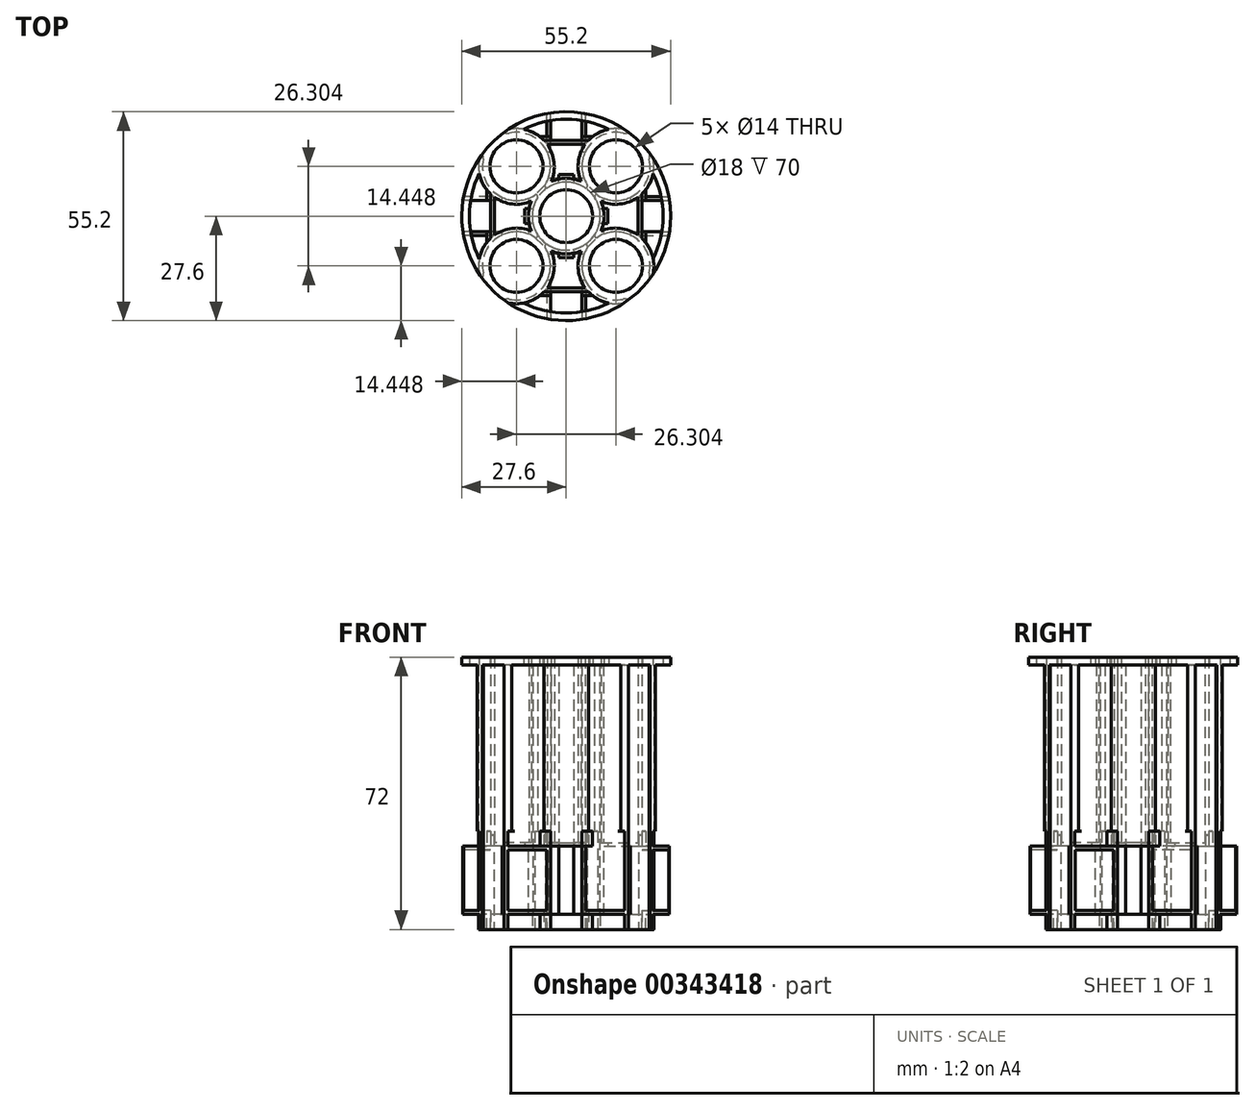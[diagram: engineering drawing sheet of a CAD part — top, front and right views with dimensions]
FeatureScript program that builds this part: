
annotation { "Feature Type Name" : "Feature", "Feature Type Description" : "" }
export const myFeature = defineFeature(function(context is Context, id is Id, definition is map)
    precondition{}
    {
        {
            var Q0;
            Q0=qCreatedBy(makeId("Top.planeOp"),FACE);
            var sketch = newSketch(context, id + "F0", { "sketchPlane" : qUnion([Q0])});
            skCircle(sketch, "E0", {"center": v(0, 0) * mm, "radius": 27.6 * mm});
            skCircle(sketch, "E1.0", {"center": v(0, 0) * mm, "radius": 28.6 * mm, "construction": true});
            skSolve(sketch);
        }
        {
            var Q0;
            Q0=qCreatedBy(makeId("Top.planeOp"),FACE);
            var sketch = newSketch(context, id + "F1", { "sketchPlane" : qUnion([Q0])});
            skCircle(sketch, "E2", {"center": v(13.15, 13.15) * mm, "radius": 9 * mm, "construction": true});
            skLineSegment(sketch, "E3", {"start": v(13.15, 13.15) * mm, "end": v(13.15, 0) * mm, "construction": true});
            skLineSegment(sketch, "E4", {"start": v(13.15, 13.15) * mm, "end": v(0, 13.15) * mm, "construction": true});
            skCircle(sketch, "E5.0", {"center": v(13.15, 13.15) * mm, "radius": 10 * mm, "construction": true});
            skCircle(sketch, "E6.1.0", {"center": v(-13.15, 13.15) * mm, "radius": 9 * mm, "construction": true});
            skCircle(sketch, "E6.1.1", {"center": v(-13.15, 13.15) * mm, "radius": 10 * mm, "construction": true});
            skCircle(sketch, "E6.2.0", {"center": v(-13.15, -13.15) * mm, "radius": 9 * mm, "construction": true});
            skCircle(sketch, "E6.2.1", {"center": v(-13.15, -13.15) * mm, "radius": 10 * mm, "construction": true});
            skCircle(sketch, "E6.3.0", {"center": v(13.15, -13.15) * mm, "radius": 9 * mm, "construction": true});
            skCircle(sketch, "E6.3.1", {"center": v(13.15, -13.15) * mm, "radius": 10 * mm, "construction": true});
            skPoint(sketch, "E6.center", {"position": v(0, 0) * mm});
            skCircle(sketch, "E7.0", {"center": v(0, 0) * mm, "radius": 9 * mm, "construction": true});
            skCircle(sketch, "E8.0", {"center": v(0, 0) * mm, "radius": 10 * mm, "construction": true});
            skSolve(sketch);
        }
        {
            var Q0;
            Q0=qCreatedBy(makeId("Top.planeOp"),FACE);
            var sketch = newSketch(context, id + "F2", { "sketchPlane" : qUnion([Q0])});
            skLineSegment(sketch, "E9.top", {"start": v(-4.13, 27) * mm, "end": v(4.12, 27) * mm, "construction": true});
            skLineSegment(sketch, "E9.left", {"start": v(-4.12, 10) * mm, "end": v(-4.13, 27) * mm, "construction": true});
            skLineSegment(sketch, "E9.right", {"start": v(4.13, 10) * mm, "end": v(4.13, 27) * mm, "construction": true});
            skPoint(sketch, "E9.middle", {"position": v(0, 18.5) * mm});
            skLineSegment(sketch, "E10", {"start": v(5.86, 20) * mm, "end": v(-5.86, 20) * mm, "construction": true});
            skLineSegment(sketch, "E11.top", {"start": v(3, 30) * mm, "end": v(-3, 30) * mm, "construction": true});
            skLineSegment(sketch, "E11.left", {"start": v(3, 27) * mm, "end": v(3, 30) * mm, "construction": true});
            skLineSegment(sketch, "E11.right", {"start": v(-3, 27) * mm, "end": v(-3, 30) * mm, "construction": true});
            skPoint(sketch, "E11.middle", {"position": v(0, 28.5) * mm});
            skLineSegment(sketch, "E12.1.4", {"start": v(-19, -5) * mm, "end": v(-19, -5) * mm});
            skLineSegment(sketch, "E12.2.4", {"start": v(5, -19) * mm, "end": v(5, -19) * mm});
            skLineSegment(sketch, "E12.3.4", {"start": v(19, 5) * mm, "end": v(19, 5) * mm});
            skLineSegment(sketch, "E13", {"start": v(-6.95, 21) * mm, "end": v(6.95, 21) * mm, "construction": true});
            skLineSegment(sketch, "E14", {"start": v(5.13, 21) * mm, "end": v(5.13, 27.12) * mm, "construction": true});
            skLineSegment(sketch, "E15.MirrorCS", {"start": v(-5.13, 21) * mm, "end": v(-5.13, 27.12) * mm, "construction": true});
            skLineSegment(sketch, "E16.top", {"start": v(2, 11) * mm, "end": v(-2, 11) * mm, "construction": true});
            skLineSegment(sketch, "E16.left", {"start": v(2, 10) * mm, "end": v(2, 11) * mm, "construction": true});
            skLineSegment(sketch, "E16.right", {"start": v(-2, 10) * mm, "end": v(-2, 11) * mm, "construction": true});
            skPoint(sketch, "E16.middle", {"position": v(0, 10.5) * mm});
            skLineSegment(sketch, "E17", {"start": v(-2, 10) * mm, "end": v(-2, 8.77) * mm, "construction": true});
            skLineSegment(sketch, "E18", {"start": v(2, 10) * mm, "end": v(2, 8.77) * mm, "construction": true});
            skLineSegment(sketch, "E19", {"start": v(4.13, 10) * mm, "end": v(-4.12, 10) * mm, "construction": true});
            skArc(sketch, "E20", {"start": v(-2, 8.77) * mm, "mid": v(0, 6.77) * mm, "end": v(2, 8.77) * mm, "construction": true});
            skLineSegment(sketch, "E21", {"start": v(-5.04, 19) * mm, "end": v(5.04, 19) * mm, "construction": true});
            skSolve(sketch);
        }
        {
            var Q0;
            Q0=qCreatedBy(makeId("Top.planeOp"),FACE);
            var sketch = newSketch(context, id + "F3", { "sketchPlane" : qUnion([Q0])});
            skArc(sketch, "E22", {"start": v(17.22, 22.83) * mm, "mid": v(20.22, 20.22) * mm, "end": v(22.83, 17.22) * mm});
            skArc(sketch, "E23", {"start": v(15.01, 21.96) * mm, "mid": v(5.75, 18.27) * mm, "end": v(5.57, 8.3) * mm});
            skPoint(sketch, "E24", {"position": v(5.57, 8.3) * mm});
            skPoint(sketch, "E25", {"position": v(8.3, 5.57) * mm});
            skLineSegment(sketch, "E26", {"start": v(5.57, 8.3) * mm, "end": v(8.3, 5.57) * mm});
            skArc(sketch, "E27.trimOffspring", {"start": v(8.3, 5.57) * mm, "mid": v(18.27, 5.75) * mm, "end": v(21.96, 15.01) * mm});
            skLineSegment(sketch, "E28", {"start": v(21.96, 15.01) * mm, "end": v(22.78, 15.58) * mm, "construction": true});
            skLineSegment(sketch, "E29", {"start": v(15.01, 21.96) * mm, "end": v(15.58, 22.78) * mm, "construction": true});
            skArc(sketch, "E30", {"start": v(15.01, 21.96) * mm, "mid": v(16.25, 22.06) * mm, "end": v(17.22, 22.83) * mm});
            skArc(sketch, "E31", {"start": v(22.83, 17.22) * mm, "mid": v(22.06, 16.25) * mm, "end": v(21.96, 15.01) * mm});
            skPoint(sketch, "E32.1.0", {"position": v(-8.3, 5.57) * mm});
            skPoint(sketch, "E32.1.1", {"position": v(-5.57, 8.3) * mm});
            skArc(sketch, "E32.1.2", {"start": v(-5.57, 8.3) * mm, "mid": v(-5.75, 18.27) * mm, "end": v(-15.01, 21.96) * mm});
            skArc(sketch, "E32.1.3", {"start": v(-21.96, 15.01) * mm, "mid": v(-18.27, 5.75) * mm, "end": v(-8.3, 5.57) * mm});
            skLineSegment(sketch, "E32.1.4", {"start": v(-15.01, 21.96) * mm, "end": v(-15.58, 22.78) * mm, "construction": true});
            skArc(sketch, "E32.1.5", {"start": v(-21.96, 15.01) * mm, "mid": v(-22.06, 16.25) * mm, "end": v(-22.83, 17.22) * mm});
            skLineSegment(sketch, "E32.1.6", {"start": v(-21.96, 15.01) * mm, "end": v(-22.78, 15.58) * mm, "construction": true});
            skArc(sketch, "E32.1.7", {"start": v(-17.22, 22.83) * mm, "mid": v(-16.25, 22.06) * mm, "end": v(-15.01, 21.96) * mm});
            skArc(sketch, "E32.1.8", {"start": v(-22.83, 17.22) * mm, "mid": v(-20.22, 20.22) * mm, "end": v(-17.22, 22.83) * mm});
            skLineSegment(sketch, "E32.1.9", {"start": v(-8.3, 5.57) * mm, "end": v(-5.57, 8.3) * mm});
            skPoint(sketch, "E32.2.0", {"position": v(-5.57, -8.3) * mm});
            skPoint(sketch, "E32.2.1", {"position": v(-8.3, -5.57) * mm});
            skArc(sketch, "E32.2.2", {"start": v(-8.3, -5.57) * mm, "mid": v(-18.27, -5.75) * mm, "end": v(-21.96, -15.01) * mm});
            skArc(sketch, "E32.2.3", {"start": v(-15.01, -21.96) * mm, "mid": v(-5.75, -18.27) * mm, "end": v(-5.57, -8.3) * mm});
            skLineSegment(sketch, "E32.2.4", {"start": v(-21.96, -15.01) * mm, "end": v(-22.78, -15.58) * mm, "construction": true});
            skArc(sketch, "E32.2.5", {"start": v(-15.01, -21.96) * mm, "mid": v(-16.25, -22.06) * mm, "end": v(-17.22, -22.83) * mm});
            skLineSegment(sketch, "E32.2.6", {"start": v(-15.01, -21.96) * mm, "end": v(-15.58, -22.78) * mm, "construction": true});
            skArc(sketch, "E32.2.7", {"start": v(-22.83, -17.22) * mm, "mid": v(-22.06, -16.25) * mm, "end": v(-21.96, -15.01) * mm});
            skArc(sketch, "E32.2.8", {"start": v(-17.22, -22.83) * mm, "mid": v(-20.22, -20.22) * mm, "end": v(-22.83, -17.22) * mm});
            skLineSegment(sketch, "E32.2.9", {"start": v(-5.57, -8.3) * mm, "end": v(-8.3, -5.57) * mm});
            skPoint(sketch, "E32.3.0", {"position": v(8.3, -5.57) * mm});
            skPoint(sketch, "E32.3.1", {"position": v(5.57, -8.3) * mm});
            skArc(sketch, "E32.3.2", {"start": v(5.57, -8.3) * mm, "mid": v(5.75, -18.27) * mm, "end": v(15.01, -21.96) * mm});
            skArc(sketch, "E32.3.3", {"start": v(21.96, -15.01) * mm, "mid": v(18.27, -5.75) * mm, "end": v(8.3, -5.57) * mm});
            skLineSegment(sketch, "E32.3.4", {"start": v(15.01, -21.96) * mm, "end": v(15.58, -22.78) * mm, "construction": true});
            skArc(sketch, "E32.3.5", {"start": v(21.96, -15.01) * mm, "mid": v(22.06, -16.25) * mm, "end": v(22.83, -17.22) * mm});
            skLineSegment(sketch, "E32.3.6", {"start": v(21.96, -15.01) * mm, "end": v(22.78, -15.58) * mm, "construction": true});
            skArc(sketch, "E32.3.7", {"start": v(17.22, -22.83) * mm, "mid": v(16.25, -22.06) * mm, "end": v(15.01, -21.96) * mm});
            skArc(sketch, "E32.3.8", {"start": v(22.83, -17.22) * mm, "mid": v(20.22, -20.22) * mm, "end": v(17.22, -22.83) * mm});
            skLineSegment(sketch, "E32.3.9", {"start": v(8.3, -5.57) * mm, "end": v(5.57, -8.3) * mm});
            skCircle(sketch, "E33.0", {"center": v(0, 0) * mm, "radius": 9 * mm});
            skSolve(sketch);
        }
        {
            var Q0;
            Q0=qCreatedBy(makeId("Top.planeOp"),FACE);
            var sketch = newSketch(context, id + "F4", { "sketchPlane" : qUnion([Q0])});
            skLineSegment(sketch, "E34.0", {"start": v(-4.12, 20) * mm, "end": v(-4.13, 21) * mm});
            skLineSegment(sketch, "E35.0", {"start": v(4.13, 20) * mm, "end": v(4.13, 21) * mm});
            skPoint(sketch, "E36.0", {"position": v(0, 18.5) * mm});
            skLineSegment(sketch, "E37.0", {"start": v(4.13, 20) * mm, "end": v(-4.12, 20) * mm});
            skLineSegment(sketch, "E38.0", {"start": v(-6.95, 21) * mm, "end": v(-4.13, 21) * mm});
            skLineSegment(sketch, "E39.trimOffspring", {"start": v(4.13, 21) * mm, "end": v(6.95, 21) * mm});
            skArc(sketch, "E40.0", {"start": v(15.98, 23.72) * mm, "mid": v(0, 28.6) * mm, "end": v(-15.98, 23.72) * mm});
            skArc(sketch, "E41.0", {"start": v(15.42, 22.9) * mm, "mid": v(10.97, 22.91) * mm, "end": v(6.95, 21) * mm});
            skLineSegment(sketch, "E42", {"start": v(15.42, 22.9) * mm, "end": v(15.98, 23.72) * mm});
            skLineSegment(sketch, "E43", {"start": v(-15.42, 22.9) * mm, "end": v(-15.98, 23.72) * mm});
            skArc(sketch, "E44.trimOffspring", {"start": v(-6.95, 21) * mm, "mid": v(-10.97, 22.91) * mm, "end": v(-15.42, 22.9) * mm});
            skArc(sketch, "E45.1.0", {"start": v(-23.72, 15.98) * mm, "mid": v(-28.6, 0) * mm, "end": v(-23.72, -15.98) * mm});
            skLineSegment(sketch, "E45.1.1", {"start": v(-20, -4.12) * mm, "end": v(-21, -4.13) * mm});
            skLineSegment(sketch, "E45.1.2", {"start": v(-22.9, -15.42) * mm, "end": v(-23.72, -15.98) * mm});
            skArc(sketch, "E45.1.3", {"start": v(-21, -6.95) * mm, "mid": v(-22.91, -10.97) * mm, "end": v(-22.9, -15.42) * mm});
            skLineSegment(sketch, "E45.1.4", {"start": v(-21, -6.95) * mm, "end": v(-21, -4.13) * mm});
            skArc(sketch, "E45.1.5", {"start": v(-22.9, 15.42) * mm, "mid": v(-22.91, 10.97) * mm, "end": v(-21, 6.95) * mm});
            skPoint(sketch, "E45.1.6", {"position": v(-18.5, 0) * mm});
            skLineSegment(sketch, "E45.1.7", {"start": v(-20, 4.13) * mm, "end": v(-21, 4.13) * mm});
            skLineSegment(sketch, "E45.1.8", {"start": v(-20, 4.13) * mm, "end": v(-20, -4.12) * mm});
            skLineSegment(sketch, "E45.1.9", {"start": v(-21, 4.13) * mm, "end": v(-21, 6.95) * mm});
            skLineSegment(sketch, "E45.1.10", {"start": v(-20, 4.13) * mm, "end": v(-21, 4.13) * mm});
            skLineSegment(sketch, "E45.1.11", {"start": v(-22.9, 15.42) * mm, "end": v(-23.72, 15.98) * mm});
            skArc(sketch, "E45.2.0", {"start": v(-15.98, -23.72) * mm, "mid": v(0, -28.6) * mm, "end": v(15.98, -23.72) * mm});
            skLineSegment(sketch, "E45.2.1", {"start": v(4.12, -20) * mm, "end": v(4.12, -21) * mm});
            skLineSegment(sketch, "E45.2.2", {"start": v(15.42, -22.9) * mm, "end": v(15.98, -23.72) * mm});
            skArc(sketch, "E45.2.3", {"start": v(6.95, -21) * mm, "mid": v(10.97, -22.91) * mm, "end": v(15.42, -22.9) * mm});
            skLineSegment(sketch, "E45.2.4", {"start": v(6.95, -21) * mm, "end": v(4.12, -21) * mm});
            skArc(sketch, "E45.2.5", {"start": v(-15.42, -22.9) * mm, "mid": v(-10.97, -22.91) * mm, "end": v(-6.95, -21) * mm});
            skPoint(sketch, "E45.2.6", {"position": v(0, -18.5) * mm});
            skLineSegment(sketch, "E45.2.7", {"start": v(-4.13, -20) * mm, "end": v(-4.13, -21) * mm});
            skLineSegment(sketch, "E45.2.8", {"start": v(-4.13, -20) * mm, "end": v(4.12, -20) * mm});
            skLineSegment(sketch, "E45.2.9", {"start": v(-4.13, -21) * mm, "end": v(-6.95, -21) * mm});
            skLineSegment(sketch, "E45.2.10", {"start": v(-4.13, -20) * mm, "end": v(-4.13, -21) * mm});
            skLineSegment(sketch, "E45.2.11", {"start": v(-15.42, -22.9) * mm, "end": v(-15.98, -23.72) * mm});
            skArc(sketch, "E45.3.0", {"start": v(23.72, -15.98) * mm, "mid": v(28.6, 0) * mm, "end": v(23.72, 15.98) * mm});
            skLineSegment(sketch, "E45.3.1", {"start": v(20, 4.13) * mm, "end": v(21, 4.13) * mm});
            skLineSegment(sketch, "E45.3.2", {"start": v(22.9, 15.42) * mm, "end": v(23.72, 15.98) * mm});
            skArc(sketch, "E45.3.3", {"start": v(21, 6.95) * mm, "mid": v(22.91, 10.97) * mm, "end": v(22.9, 15.42) * mm});
            skLineSegment(sketch, "E45.3.4", {"start": v(21, 6.95) * mm, "end": v(21, 4.13) * mm});
            skArc(sketch, "E45.3.5", {"start": v(22.9, -15.42) * mm, "mid": v(22.91, -10.97) * mm, "end": v(21, -6.95) * mm});
            skPoint(sketch, "E45.3.6", {"position": v(18.5, 0) * mm});
            skLineSegment(sketch, "E45.3.7", {"start": v(20, -4.12) * mm, "end": v(21, -4.12) * mm});
            skLineSegment(sketch, "E45.3.8", {"start": v(20, -4.12) * mm, "end": v(20, 4.12) * mm});
            skLineSegment(sketch, "E45.3.9", {"start": v(21, -4.12) * mm, "end": v(21, -6.95) * mm});
            skLineSegment(sketch, "E45.3.10", {"start": v(20, -4.12) * mm, "end": v(21, -4.12) * mm});
            skLineSegment(sketch, "E45.3.11", {"start": v(22.9, -15.42) * mm, "end": v(23.72, -15.98) * mm});
            skSolve(sketch);
        }
        {
            var Q0;
            Q0=qCreatedBy(makeId("Top.planeOp"),FACE);
            var sketch = newSketch(context, id + "F5", { "sketchPlane" : qUnion([Q0])});
            skArc(sketch, "E46.0", {"start": v(-2, 8.77) * mm, "mid": v(0, 6.77) * mm, "end": v(2, 8.77) * mm});
            skLineSegment(sketch, "E47.0", {"start": v(2, 11) * mm, "end": v(-2, 11) * mm});
            skLineSegment(sketch, "E48.0", {"start": v(2, 10) * mm, "end": v(2, 11) * mm});
            skLineSegment(sketch, "E49.0", {"start": v(2, 10) * mm, "end": v(2, 8.77) * mm});
            skLineSegment(sketch, "E50.0", {"start": v(-2, 10) * mm, "end": v(-2, 8.77) * mm});
            skLineSegment(sketch, "E51.0", {"start": v(-2, 10) * mm, "end": v(-2, 11) * mm});
            skArc(sketch, "E52.1.0", {"start": v(-8.77, -2) * mm, "mid": v(-6.77, 0) * mm, "end": v(-8.77, 2) * mm});
            skLineSegment(sketch, "E52.1.1", {"start": v(-11, 2) * mm, "end": v(-11, -2) * mm});
            skLineSegment(sketch, "E52.1.2", {"start": v(-10, 2) * mm, "end": v(-11, 2) * mm});
            skLineSegment(sketch, "E52.1.3", {"start": v(-10, -2) * mm, "end": v(-11, -2) * mm});
            skLineSegment(sketch, "E52.1.4", {"start": v(-10, 2) * mm, "end": v(-8.77, 2) * mm});
            skLineSegment(sketch, "E52.1.5", {"start": v(-10, -2) * mm, "end": v(-8.77, -2) * mm});
            skArc(sketch, "E52.2.0", {"start": v(2, -8.77) * mm, "mid": v(0, -6.77) * mm, "end": v(-2, -8.77) * mm});
            skLineSegment(sketch, "E52.2.1", {"start": v(-2, -11) * mm, "end": v(2, -11) * mm});
            skLineSegment(sketch, "E52.2.2", {"start": v(-2, -10) * mm, "end": v(-2, -11) * mm});
            skLineSegment(sketch, "E52.2.3", {"start": v(2, -10) * mm, "end": v(2, -11) * mm});
            skLineSegment(sketch, "E52.2.4", {"start": v(-2, -10) * mm, "end": v(-2, -8.77) * mm});
            skLineSegment(sketch, "E52.2.5", {"start": v(2, -10) * mm, "end": v(2, -8.77) * mm});
            skArc(sketch, "E52.3.0", {"start": v(8.77, 2) * mm, "mid": v(6.77, 0) * mm, "end": v(8.77, -2) * mm});
            skLineSegment(sketch, "E52.3.1", {"start": v(11, -2) * mm, "end": v(11, 2) * mm});
            skLineSegment(sketch, "E52.3.2", {"start": v(10, -2) * mm, "end": v(11, -2) * mm});
            skLineSegment(sketch, "E52.3.3", {"start": v(10, 2) * mm, "end": v(11, 2) * mm});
            skLineSegment(sketch, "E52.3.4", {"start": v(10, -2) * mm, "end": v(8.77, -2) * mm});
            skLineSegment(sketch, "E52.3.5", {"start": v(10, 2) * mm, "end": v(8.77, 2) * mm});
            skPoint(sketch, "E52.center", {"position": v(0, 0) * mm});
            skSolve(sketch);
        }
        {
            var Q0;
            Q0=qCreatedBy(makeId("Top.planeOp"),FACE);
            var sketch = newSketch(context, id + "F6", { "sketchPlane" : qUnion([Q0])});
            skLineSegment(sketch, "E53.0", {"start": v(-4.12, 17.45) * mm, "end": v(-4.13, 27.3) * mm});
            skLineSegment(sketch, "E54.0", {"start": v(4.13, 17.45) * mm, "end": v(4.13, 27.3) * mm});
            skArc(sketch, "E55.0", {"start": v(3.1, 28.43) * mm, "mid": v(0, 28.6) * mm, "end": v(-3.1, 28.43) * mm});
            skArc(sketch, "E56", {"start": v(-4.13, 27.3) * mm, "mid": v(-3.83, 28.06) * mm, "end": v(-3.1, 28.43) * mm});
            skArc(sketch, "E57", {"start": v(4.13, 27.3) * mm, "mid": v(3.83, 28.06) * mm, "end": v(3.1, 28.43) * mm});
            skPoint(sketch, "E58.0", {"position": v(0, 18.5) * mm});
            skLineSegment(sketch, "E59.0", {"start": v(4.72, 10) * mm, "end": v(-4.72, 10) * mm});
            skArc(sketch, "E60.0", {"start": v(-4.72, 10) * mm, "mid": v(-4.17, 13.65) * mm, "end": v(-5.12, 17.22) * mm});
            skArc(sketch, "E61.0", {"start": v(5.12, 17.22) * mm, "mid": v(4.17, 13.65) * mm, "end": v(4.72, 10) * mm});
            skArc(sketch, "E62", {"start": v(-5.12, 17.22) * mm, "mid": v(-4.53, 16.94) * mm, "end": v(-4.12, 17.45) * mm});
            skLineSegment(sketch, "E63", {"start": v(-4.98, 9.37) * mm, "end": v(-4.98, 9.37) * mm});
            skArc(sketch, "E64", {"start": v(4.12, 17.45) * mm, "mid": v(4.53, 16.94) * mm, "end": v(5.12, 17.22) * mm});
            skArc(sketch, "E65.1.0", {"start": v(-28.43, 3.1) * mm, "mid": v(-28.6, 0) * mm, "end": v(-28.43, -3.1) * mm});
            skPoint(sketch, "E65.1.1", {"position": v(-18.5, 0) * mm});
            skArc(sketch, "E65.1.2", {"start": v(-10, -4.72) * mm, "mid": v(-13.65, -4.17) * mm, "end": v(-17.22, -5.12) * mm});
            skLineSegment(sketch, "E65.1.3", {"start": v(-10, 4.72) * mm, "end": v(-10, -4.72) * mm});
            skLineSegment(sketch, "E65.1.4", {"start": v(-17.45, -4.12) * mm, "end": v(-27.3, -4.12) * mm});
            skArc(sketch, "E65.1.5", {"start": v(-17.22, -5.12) * mm, "mid": v(-16.94, -4.53) * mm, "end": v(-17.45, -4.13) * mm});
            skArc(sketch, "E65.1.6", {"start": v(-17.22, 5.12) * mm, "mid": v(-13.65, 4.17) * mm, "end": v(-10, 4.72) * mm});
            skArc(sketch, "E65.1.7", {"start": v(-17.45, 4.12) * mm, "mid": v(-16.94, 4.53) * mm, "end": v(-17.22, 5.12) * mm});
            skArc(sketch, "E65.1.8", {"start": v(-27.3, -4.13) * mm, "mid": v(-28.06, -3.83) * mm, "end": v(-28.43, -3.1) * mm});
            skLineSegment(sketch, "E65.1.9", {"start": v(-17.45, 4.13) * mm, "end": v(-27.3, 4.13) * mm});
            skLineSegment(sketch, "E65.1.10", {"start": v(-17.45, 4.13) * mm, "end": v(-27.3, 4.13) * mm});
            skArc(sketch, "E65.1.11", {"start": v(-27.3, 4.13) * mm, "mid": v(-28.06, 3.83) * mm, "end": v(-28.43, 3.1) * mm});
            skArc(sketch, "E65.2.0", {"start": v(-3.1, -28.43) * mm, "mid": v(0, -28.6) * mm, "end": v(3.1, -28.43) * mm});
            skPoint(sketch, "E65.2.1", {"position": v(0, -18.5) * mm});
            skArc(sketch, "E65.2.2", {"start": v(4.72, -10) * mm, "mid": v(4.17, -13.65) * mm, "end": v(5.12, -17.22) * mm});
            skLineSegment(sketch, "E65.2.3", {"start": v(-4.72, -10) * mm, "end": v(4.72, -10) * mm});
            skLineSegment(sketch, "E65.2.4", {"start": v(4.12, -17.45) * mm, "end": v(4.13, -27.3) * mm});
            skArc(sketch, "E65.2.5", {"start": v(5.12, -17.22) * mm, "mid": v(4.53, -16.94) * mm, "end": v(4.12, -17.45) * mm});
            skArc(sketch, "E65.2.6", {"start": v(-5.12, -17.22) * mm, "mid": v(-4.17, -13.65) * mm, "end": v(-4.72, -10) * mm});
            skArc(sketch, "E65.2.7", {"start": v(-4.12, -17.45) * mm, "mid": v(-4.53, -16.94) * mm, "end": v(-5.12, -17.22) * mm});
            skArc(sketch, "E65.2.8", {"start": v(4.12, -27.3) * mm, "mid": v(3.83, -28.06) * mm, "end": v(3.1, -28.43) * mm});
            skLineSegment(sketch, "E65.2.9", {"start": v(-4.13, -17.45) * mm, "end": v(-4.13, -27.3) * mm});
            skLineSegment(sketch, "E65.2.10", {"start": v(-4.13, -17.45) * mm, "end": v(-4.13, -27.3) * mm});
            skArc(sketch, "E65.2.11", {"start": v(-4.13, -27.3) * mm, "mid": v(-3.83, -28.06) * mm, "end": v(-3.1, -28.43) * mm});
            skArc(sketch, "E65.3.0", {"start": v(28.43, -3.1) * mm, "mid": v(28.6, 0) * mm, "end": v(28.43, 3.1) * mm});
            skPoint(sketch, "E65.3.1", {"position": v(18.5, 0) * mm});
            skArc(sketch, "E65.3.2", {"start": v(10, 4.72) * mm, "mid": v(13.65, 4.17) * mm, "end": v(17.22, 5.12) * mm});
            skLineSegment(sketch, "E65.3.3", {"start": v(10, -4.72) * mm, "end": v(10, 4.72) * mm});
            skLineSegment(sketch, "E65.3.4", {"start": v(17.45, 4.13) * mm, "end": v(27.3, 4.13) * mm});
            skArc(sketch, "E65.3.5", {"start": v(17.22, 5.12) * mm, "mid": v(16.94, 4.53) * mm, "end": v(17.45, 4.13) * mm});
            skArc(sketch, "E65.3.6", {"start": v(17.22, -5.12) * mm, "mid": v(13.65, -4.17) * mm, "end": v(10, -4.72) * mm});
            skArc(sketch, "E65.3.7", {"start": v(17.45, -4.12) * mm, "mid": v(16.94, -4.53) * mm, "end": v(17.22, -5.12) * mm});
            skArc(sketch, "E65.3.8", {"start": v(27.3, 4.13) * mm, "mid": v(28.06, 3.83) * mm, "end": v(28.43, 3.1) * mm});
            skLineSegment(sketch, "E65.3.9", {"start": v(17.45, -4.13) * mm, "end": v(27.3, -4.13) * mm});
            skLineSegment(sketch, "E65.3.10", {"start": v(17.45, -4.13) * mm, "end": v(27.3, -4.13) * mm});
            skArc(sketch, "E65.3.11", {"start": v(27.3, -4.13) * mm, "mid": v(28.06, -3.83) * mm, "end": v(28.43, -3.1) * mm});
            skSolve(sketch);
        }
        {
            var Q0;
            Q0=qCreatedBy(makeId("Top.planeOp"),FACE);
            cPlane(context, id + "F7", {"entities" : qUnion([Q0]), "cplaneType" : CPlaneType.OFFSET, "offset" : 13 * mm, "width" : 150 * mm, "height" : 150 * mm});
        }
        {
            var Q0;
            Q0=qCreatedBy(makeId("Top.planeOp"),FACE);
            cPlane(context, id + "F8", {"entities" : qUnion([Q0]), "cplaneType" : CPlaneType.OFFSET, "offset" : 13 * mm, "oppositeDirection" : true, "width" : 150 * mm, "height" : 150 * mm});
        }
        {
            var Q0;
            Q0 = qSketchRegion(id + "F0", true);
            extrude(context, id + "F9", {"entities" : qUnion([Q0]), "endBound" : BoundingType.SYMMETRIC, "depth" : 26 * mm});
        }
        {
            var Q0;
            Q0 = qSketchRegion(id + "F3", true);
            extrude(context, id + "F10", {"entities" : qUnion([Q0]), "operationType" : NewBodyOperationType.REMOVE, "endBound" : BoundingType.SYMMETRIC, "depth" : 28 * mm});
        }
        {
            var Q0;
            Q0 = qSketchRegion(id + "F4", true);
            extrude(context, id + "F11", {"entities" : qUnion([Q0]), "operationType" : NewBodyOperationType.REMOVE, "endBound" : BoundingType.THROUGH_ALL, "oppositeDirection" : true, "depth" : 20.8 * mm, "hasSecondDirection" : true, "secondDirectionOppositeDirection" : true, "secondDirectionDepth" : 9 * mm});
        }
        {
            var Q0;
            Q0 = qSketchRegion(id + "F4", true);
            extrude(context, id + "F12", {"entities" : qUnion([Q0]), "operationType" : NewBodyOperationType.REMOVE, "endBound" : BoundingType.THROUGH_ALL, "depth" : 25 * mm, "hasSecondDirection" : true, "secondDirectionOppositeDirection" : false, "secondDirectionDepth" : 9 * mm});
        }
        {
            var Q0;
            Q0 = qSketchRegion(id + "F6", true);
            extrude(context, id + "F13", {"entities" : qUnion([Q0]), "operationType" : NewBodyOperationType.REMOVE, "endBound" : BoundingType.SYMMETRIC, "oppositeDirection" : true, "depth" : 18 * mm});
        }
        {
            var Q0;
            Q0=qCreatedBy(id+"F7.planeOp",FACE);
            var sketch = newSketch(context, id + "F14", { "sketchPlane" : qUnion([Q0])});
            skArc(sketch, "E66.0", {"start": v(15.01, 21.96) * mm, "mid": v(5.75, 18.27) * mm, "end": v(5.57, 8.3) * mm});
            skArc(sketch, "E67.0", {"start": v(23.53, 14.43) * mm, "mid": v(22.86, 15.46) * mm, "end": v(22.16, 16.46) * mm});
            skArc(sketch, "E68.0", {"start": v(15.01, 21.96) * mm, "mid": v(15.75, 21.93) * mm, "end": v(16.46, 22.16) * mm});
            skArc(sketch, "E69.0", {"start": v(22.16, 16.46) * mm, "mid": v(21.93, 15.75) * mm, "end": v(21.96, 15.01) * mm});
            skLineSegment(sketch, "E70", {"start": v(14.43, 23.53) * mm, "end": v(14.43, 23.53) * mm});
            skPoint(sketch, "E71.visualSharp", {"position": v(14.17, 23.1) * mm});
            skArc(sketch, "E71.filletArc", {"start": v(13.7, 23.14) * mm, "mid": v(14.11, 23.23) * mm, "end": v(14.43, 23.53) * mm});
            skLineSegment(sketch, "E72", {"start": v(23.53, 14.43) * mm, "end": v(23.53, 14.43) * mm});
            skPoint(sketch, "E73.newPointB", {"position": v(23.1, 14.17) * mm});
            skArc(sketch, "E73.filletArc", {"start": v(23.53, 14.43) * mm, "mid": v(23.23, 14.11) * mm, "end": v(23.14, 13.7) * mm});
            skArc(sketch, "E74.trimOffspring", {"start": v(8.3, 5.57) * mm, "mid": v(18.27, 5.75) * mm, "end": v(21.96, 15.01) * mm});
            skLineSegment(sketch, "E75.trimOffspring", {"start": v(9.18, 3.98) * mm, "end": v(9.18, 3.98) * mm});
            skArc(sketch, "E76", {"start": v(4.85, 7.58) * mm, "mid": v(5.5, 7.65) * mm, "end": v(5.57, 8.3) * mm});
            skArc(sketch, "E77", {"start": v(8.3, 5.57) * mm, "mid": v(7.65, 5.5) * mm, "end": v(7.58, 4.85) * mm});
            skArc(sketch, "E78.trimOffspring", {"start": v(9.18, 3.98) * mm, "mid": v(18.86, 4.94) * mm, "end": v(23.14, 13.7) * mm});
            skArc(sketch, "E79.0", {"start": v(3.98, 9.18) * mm, "mid": v(2.03, 9.8) * mm, "end": v(0, 10) * mm});
            skArc(sketch, "E80.trimOffspring", {"start": v(10, 0) * mm, "mid": v(9.8, 2.03) * mm, "end": v(9.18, 3.98) * mm});
            skArc(sketch, "E81.trimOffspring", {"start": v(16.46, 22.16) * mm, "mid": v(15.46, 22.86) * mm, "end": v(14.43, 23.53) * mm});
            skArc(sketch, "E82.0", {"start": v(4.85, 7.58) * mm, "mid": v(2.52, 8.64) * mm, "end": v(0, 9) * mm});
            skArc(sketch, "E83.trimOffspring", {"start": v(9, 0) * mm, "mid": v(8.64, 2.52) * mm, "end": v(7.58, 4.85) * mm});
            skArc(sketch, "E84.0", {"start": v(13.7, 23.14) * mm, "mid": v(4.94, 18.86) * mm, "end": v(3.98, 9.18) * mm});
            skSolve(sketch);
        }
        {
            var Q0;
            Q0=qCreatedBy(id+"F7.planeOp",FACE);
            var sketch = newSketch(context, id + "F15", { "sketchPlane" : qUnion([Q0])});
            skArc(sketch, "E85.0", {"start": v(15.01, 21.96) * mm, "mid": v(5.75, 18.27) * mm, "end": v(5.57, 8.3) * mm});
            skArc(sketch, "E85.1", {"start": v(9, 0) * mm, "mid": v(8.64, 2.52) * mm, "end": v(7.58, 4.85) * mm});
            skArc(sketch, "E85.2", {"start": v(23.53, 14.43) * mm, "mid": v(22.86, 15.46) * mm, "end": v(22.16, 16.46) * mm});
            skArc(sketch, "E85.3", {"start": v(15.01, 21.96) * mm, "mid": v(15.75, 21.93) * mm, "end": v(16.46, 22.16) * mm});
            skArc(sketch, "E85.4", {"start": v(22.16, 16.46) * mm, "mid": v(21.93, 15.75) * mm, "end": v(21.96, 15.01) * mm});
            skArc(sketch, "E85.5", {"start": v(8.3, 5.57) * mm, "mid": v(18.27, 5.75) * mm, "end": v(21.96, 15.01) * mm});
            skArc(sketch, "E85.6", {"start": v(3.98, 9.18) * mm, "mid": v(2.03, 9.8) * mm, "end": v(0, 10) * mm});
            skArc(sketch, "E85.7", {"start": v(10, 0) * mm, "mid": v(9.8, 2.03) * mm, "end": v(9.18, 3.98) * mm});
            skArc(sketch, "E85.8", {"start": v(13.7, 23.14) * mm, "mid": v(4.94, 18.86) * mm, "end": v(3.98, 9.18) * mm});
            skArc(sketch, "E85.9", {"start": v(9.18, 3.98) * mm, "mid": v(18.86, 4.94) * mm, "end": v(23.14, 13.7) * mm});
            skArc(sketch, "E85.10", {"start": v(16.46, 22.16) * mm, "mid": v(15.46, 22.86) * mm, "end": v(14.43, 23.53) * mm});
            skArc(sketch, "E85.11", {"start": v(4.85, 7.58) * mm, "mid": v(2.52, 8.64) * mm, "end": v(0, 9) * mm});
            skArc(sketch, "E85.12", {"start": v(4.85, 7.58) * mm, "mid": v(5.5, 7.65) * mm, "end": v(5.57, 8.3) * mm});
            skArc(sketch, "E85.13", {"start": v(9.18, 3.98) * mm, "mid": v(18.86, 4.94) * mm, "end": v(23.14, 13.7) * mm});
            skArc(sketch, "E86.0", {"start": v(13.7, 23.14) * mm, "mid": v(14.11, 23.23) * mm, "end": v(14.43, 23.53) * mm});
            skArc(sketch, "E87.0", {"start": v(23.53, 14.43) * mm, "mid": v(23.23, 14.11) * mm, "end": v(23.14, 13.7) * mm});
            skArc(sketch, "E88.0", {"start": v(8.3, 5.57) * mm, "mid": v(7.65, 5.5) * mm, "end": v(7.58, 4.85) * mm});
            skArc(sketch, "E89.1.0", {"start": v(-5.57, 8.3) * mm, "mid": v(-5.75, 18.27) * mm, "end": v(-15.01, 21.96) * mm});
            skArc(sketch, "E89.1.1", {"start": v(-22.16, 16.46) * mm, "mid": v(-22.86, 15.46) * mm, "end": v(-23.53, 14.43) * mm});
            skArc(sketch, "E89.1.2", {"start": v(-9.18, 3.98) * mm, "mid": v(-9.8, 2.03) * mm, "end": v(-10, 0) * mm});
            skArc(sketch, "E89.1.3", {"start": v(-14.43, 23.53) * mm, "mid": v(-15.46, 22.86) * mm, "end": v(-16.46, 22.16) * mm});
            skArc(sketch, "E89.1.4", {"start": v(-23.14, 13.7) * mm, "mid": v(-18.86, 4.94) * mm, "end": v(-9.18, 3.98) * mm});
            skArc(sketch, "E89.1.5", {"start": v(-3.98, 9.18) * mm, "mid": v(-4.94, 18.86) * mm, "end": v(-13.7, 23.14) * mm});
            skArc(sketch, "E89.1.6", {"start": v(-21.96, 15.01) * mm, "mid": v(-18.27, 5.75) * mm, "end": v(-8.3, 5.57) * mm});
            skArc(sketch, "E89.1.7", {"start": v(-7.58, 4.85) * mm, "mid": v(-8.64, 2.52) * mm, "end": v(-9, 0) * mm});
            skArc(sketch, "E89.1.8", {"start": v(0, 9) * mm, "mid": v(-2.52, 8.64) * mm, "end": v(-4.85, 7.58) * mm});
            skArc(sketch, "E89.1.9", {"start": v(0, 10) * mm, "mid": v(-2.03, 9.8) * mm, "end": v(-3.98, 9.18) * mm});
            skArc(sketch, "E89.1.10", {"start": v(-3.98, 9.18) * mm, "mid": v(-4.94, 18.86) * mm, "end": v(-13.7, 23.14) * mm});
            skArc(sketch, "E89.1.11", {"start": v(-21.96, 15.01) * mm, "mid": v(-21.93, 15.75) * mm, "end": v(-22.16, 16.46) * mm});
            skArc(sketch, "E89.1.12", {"start": v(-7.58, 4.85) * mm, "mid": v(-7.65, 5.5) * mm, "end": v(-8.3, 5.57) * mm});
            skArc(sketch, "E89.1.13", {"start": v(-23.14, 13.7) * mm, "mid": v(-23.23, 14.11) * mm, "end": v(-23.53, 14.43) * mm});
            skArc(sketch, "E89.1.14", {"start": v(-5.57, 8.3) * mm, "mid": v(-5.5, 7.65) * mm, "end": v(-4.85, 7.58) * mm});
            skArc(sketch, "E89.1.15", {"start": v(-16.46, 22.16) * mm, "mid": v(-15.75, 21.93) * mm, "end": v(-15.01, 21.96) * mm});
            skArc(sketch, "E89.1.16", {"start": v(-14.43, 23.53) * mm, "mid": v(-14.11, 23.23) * mm, "end": v(-13.7, 23.14) * mm});
            skArc(sketch, "E89.2.0", {"start": v(-8.3, -5.57) * mm, "mid": v(-18.27, -5.75) * mm, "end": v(-21.96, -15.01) * mm});
            skArc(sketch, "E89.2.1", {"start": v(-16.46, -22.16) * mm, "mid": v(-15.46, -22.86) * mm, "end": v(-14.43, -23.53) * mm});
            skArc(sketch, "E89.2.2", {"start": v(-3.98, -9.18) * mm, "mid": v(-2.03, -9.8) * mm, "end": v(0, -10) * mm});
            skArc(sketch, "E89.2.3", {"start": v(-23.53, -14.43) * mm, "mid": v(-22.86, -15.46) * mm, "end": v(-22.16, -16.46) * mm});
            skArc(sketch, "E89.2.4", {"start": v(-13.7, -23.14) * mm, "mid": v(-4.94, -18.86) * mm, "end": v(-3.98, -9.18) * mm});
            skArc(sketch, "E89.2.5", {"start": v(-9.18, -3.98) * mm, "mid": v(-18.86, -4.94) * mm, "end": v(-23.14, -13.7) * mm});
            skArc(sketch, "E89.2.6", {"start": v(-15.01, -21.96) * mm, "mid": v(-5.75, -18.27) * mm, "end": v(-5.57, -8.3) * mm});
            skArc(sketch, "E89.2.7", {"start": v(-4.85, -7.58) * mm, "mid": v(-2.52, -8.64) * mm, "end": v(0, -9) * mm});
            skArc(sketch, "E89.2.8", {"start": v(-9, 0) * mm, "mid": v(-8.64, -2.52) * mm, "end": v(-7.58, -4.85) * mm});
            skArc(sketch, "E89.2.9", {"start": v(-10, 0) * mm, "mid": v(-9.8, -2.03) * mm, "end": v(-9.18, -3.98) * mm});
            skArc(sketch, "E89.2.10", {"start": v(-9.18, -3.98) * mm, "mid": v(-18.86, -4.94) * mm, "end": v(-23.14, -13.7) * mm});
            skArc(sketch, "E89.2.11", {"start": v(-15.01, -21.96) * mm, "mid": v(-15.75, -21.93) * mm, "end": v(-16.46, -22.16) * mm});
            skArc(sketch, "E89.2.12", {"start": v(-4.85, -7.58) * mm, "mid": v(-5.5, -7.65) * mm, "end": v(-5.57, -8.3) * mm});
            skArc(sketch, "E89.2.13", {"start": v(-13.7, -23.14) * mm, "mid": v(-14.11, -23.23) * mm, "end": v(-14.43, -23.53) * mm});
            skArc(sketch, "E89.2.14", {"start": v(-8.3, -5.57) * mm, "mid": v(-7.65, -5.5) * mm, "end": v(-7.58, -4.85) * mm});
            skArc(sketch, "E89.2.15", {"start": v(-22.16, -16.46) * mm, "mid": v(-21.93, -15.75) * mm, "end": v(-21.96, -15.01) * mm});
            skArc(sketch, "E89.2.16", {"start": v(-23.53, -14.43) * mm, "mid": v(-23.23, -14.11) * mm, "end": v(-23.14, -13.7) * mm});
            skArc(sketch, "E89.3.0", {"start": v(5.57, -8.3) * mm, "mid": v(5.75, -18.27) * mm, "end": v(15.01, -21.96) * mm});
            skArc(sketch, "E89.3.1", {"start": v(22.16, -16.46) * mm, "mid": v(22.86, -15.46) * mm, "end": v(23.53, -14.43) * mm});
            skArc(sketch, "E89.3.2", {"start": v(9.18, -3.98) * mm, "mid": v(9.8, -2.03) * mm, "end": v(10, 0) * mm});
            skArc(sketch, "E89.3.3", {"start": v(14.43, -23.53) * mm, "mid": v(15.46, -22.86) * mm, "end": v(16.46, -22.16) * mm});
            skArc(sketch, "E89.3.4", {"start": v(23.14, -13.7) * mm, "mid": v(18.86, -4.94) * mm, "end": v(9.18, -3.98) * mm});
            skArc(sketch, "E89.3.5", {"start": v(3.98, -9.18) * mm, "mid": v(4.94, -18.86) * mm, "end": v(13.7, -23.14) * mm});
            skArc(sketch, "E89.3.6", {"start": v(21.96, -15.01) * mm, "mid": v(18.27, -5.75) * mm, "end": v(8.3, -5.57) * mm});
            skArc(sketch, "E89.3.7", {"start": v(7.58, -4.85) * mm, "mid": v(8.64, -2.52) * mm, "end": v(9, 0) * mm});
            skArc(sketch, "E89.3.8", {"start": v(0, -9) * mm, "mid": v(2.52, -8.64) * mm, "end": v(4.85, -7.58) * mm});
            skArc(sketch, "E89.3.9", {"start": v(0, -10) * mm, "mid": v(2.03, -9.8) * mm, "end": v(3.98, -9.18) * mm});
            skArc(sketch, "E89.3.10", {"start": v(3.98, -9.18) * mm, "mid": v(4.94, -18.86) * mm, "end": v(13.7, -23.14) * mm});
            skArc(sketch, "E89.3.11", {"start": v(21.96, -15.01) * mm, "mid": v(21.93, -15.75) * mm, "end": v(22.16, -16.46) * mm});
            skArc(sketch, "E89.3.12", {"start": v(7.58, -4.85) * mm, "mid": v(7.65, -5.5) * mm, "end": v(8.3, -5.57) * mm});
            skArc(sketch, "E89.3.13", {"start": v(23.14, -13.7) * mm, "mid": v(23.23, -14.11) * mm, "end": v(23.53, -14.43) * mm});
            skArc(sketch, "E89.3.14", {"start": v(5.57, -8.3) * mm, "mid": v(5.5, -7.65) * mm, "end": v(4.85, -7.58) * mm});
            skArc(sketch, "E89.3.15", {"start": v(16.46, -22.16) * mm, "mid": v(15.75, -21.93) * mm, "end": v(15.01, -21.96) * mm});
            skArc(sketch, "E89.3.16", {"start": v(14.43, -23.53) * mm, "mid": v(14.11, -23.23) * mm, "end": v(13.7, -23.14) * mm});
            skSolve(sketch);
        }
        {
            var Q0;
            Q0=qCreatedBy(id+"F7.planeOp",FACE);
            var sketch = newSketch(context, id + "F16", { "sketchPlane" : qUnion([Q0])});
            skLineSegment(sketch, "E90.0", {"start": v(7.31, 20) * mm, "end": v(-7.31, 20) * mm});
            skLineSegment(sketch, "E91.0", {"start": v(-6.31, 19) * mm, "end": v(6.31, 19) * mm});
            skArc(sketch, "E92.0", {"start": v(7.31, 20) * mm, "mid": v(6.8, 19.52) * mm, "end": v(6.31, 19) * mm});
            skArc(sketch, "E93.0", {"start": v(-6.31, 19) * mm, "mid": v(-6.8, 19.52) * mm, "end": v(-7.31, 20) * mm});
            skPoint(sketch, "E94.orphan", {"position": v(5.86, 20) * mm});
            skPoint(sketch, "E95.orphan", {"position": v(5.04, 19) * mm});
            skPoint(sketch, "E96.orphan", {"position": v(-5.86, 20) * mm});
            skPoint(sketch, "E97.orphan", {"position": v(-5.04, 19) * mm});
            skPoint(sketch, "E98.1.0", {"position": v(-20, -5.86) * mm});
            skPoint(sketch, "E98.1.1", {"position": v(-19, -5.04) * mm});
            skLineSegment(sketch, "E98.1.2", {"start": v(-19, -6.31) * mm, "end": v(-19, 6.31) * mm});
            skLineSegment(sketch, "E98.1.3", {"start": v(-20, 7.31) * mm, "end": v(-20, -7.31) * mm});
            skPoint(sketch, "E98.1.4", {"position": v(-20, 5.86) * mm});
            skPoint(sketch, "E98.1.5", {"position": v(-19, 5.04) * mm});
            skArc(sketch, "E98.1.6", {"start": v(-19, -6.31) * mm, "mid": v(-19.52, -6.8) * mm, "end": v(-20, -7.31) * mm});
            skArc(sketch, "E98.1.7", {"start": v(-20, 7.31) * mm, "mid": v(-19.52, 6.8) * mm, "end": v(-19, 6.31) * mm});
            skPoint(sketch, "E98.2.0", {"position": v(5.86, -20) * mm});
            skPoint(sketch, "E98.2.1", {"position": v(5.04, -19) * mm});
            skLineSegment(sketch, "E98.2.2", {"start": v(6.31, -19) * mm, "end": v(-6.31, -19) * mm});
            skLineSegment(sketch, "E98.2.3", {"start": v(-7.31, -20) * mm, "end": v(7.31, -20) * mm});
            skPoint(sketch, "E98.2.4", {"position": v(-5.86, -20) * mm});
            skPoint(sketch, "E98.2.5", {"position": v(-5.04, -19) * mm});
            skArc(sketch, "E98.2.6", {"start": v(6.31, -19) * mm, "mid": v(6.8, -19.52) * mm, "end": v(7.31, -20) * mm});
            skArc(sketch, "E98.2.7", {"start": v(-7.31, -20) * mm, "mid": v(-6.8, -19.52) * mm, "end": v(-6.31, -19) * mm});
            skPoint(sketch, "E98.3.0", {"position": v(20, 5.86) * mm});
            skPoint(sketch, "E98.3.1", {"position": v(19, 5.04) * mm});
            skLineSegment(sketch, "E98.3.2", {"start": v(19, 6.31) * mm, "end": v(19, -6.31) * mm});
            skLineSegment(sketch, "E98.3.3", {"start": v(20, -7.31) * mm, "end": v(20, 7.31) * mm});
            skPoint(sketch, "E98.3.4", {"position": v(20, -5.86) * mm});
            skPoint(sketch, "E98.3.5", {"position": v(19, -5.04) * mm});
            skArc(sketch, "E98.3.6", {"start": v(19, 6.31) * mm, "mid": v(19.52, 6.8) * mm, "end": v(20, 7.31) * mm});
            skArc(sketch, "E98.3.7", {"start": v(20, -7.31) * mm, "mid": v(19.52, -6.8) * mm, "end": v(19, -6.31) * mm});
            skPoint(sketch, "E98.center", {"position": v(0, 0) * mm});
            skSolve(sketch);
        }
        {
            var Q0;
            Q0=qCreatedBy(id+"F8.planeOp",FACE);
            cPlane(context, id + "F17", {"entities" : qUnion([Q0]), "cplaneType" : CPlaneType.OFFSET, "offset" : 70 * mm, "width" : 150 * mm, "height" : 150 * mm});
        }
        {
            var Q0;
            Q0=qCreatedBy(id+"F17.planeOp",FACE);
            cPlane(context, id + "F18", {"entities" : qUnion([Q0]), "cplaneType" : CPlaneType.OFFSET, "offset" : 2 * mm, "width" : 150 * mm, "height" : 150 * mm});
        }
        {
            var Q0;
            Q0 = qSketchRegion(id + "F16", true);
            var Q1;
            Q1=qCreatedBy(id+"F18.planeOp",FACE);
            extrude(context, id + "F19", {"entities" : qUnion([Q0]), "operationType" : NewBodyOperationType.ADD, "endBound" : BoundingType.UP_TO_SURFACE, "endBoundEntityFace" : qUnion([Q1]), "depth" : 25 * mm});
        }
        {
            var Q0;
            Q0=makeQuery(id+"F19.boolean.opBoolean","SPLIT",FACE,{"disambiguationData":[TD([makeQuery(id+"F10.boolean.opBoolean","COPY",FACE,{"derivedFrom":makeQuery(id+"F10.opExtrude","SWEPT_FACE",FACE,{"disambiguationData":[OSD([sQuery(id+"F3.wireOp",EDGE,"E26")])]})})])],"derivedFrom":makeQuery(id+"F9.opExtrude","CAP_FACE",FACE,{"disambiguationData":[OSD([sQuery(id+"F0.wireOp",EDGE,"E0")])],"isStart":false})});
            var Q1;
            {var subQ0=makeQuery(id+"F10.opExtrude","SWEPT_FACE",FACE,{"disambiguationData":[OSD([sQuery(id+"F3.wireOp",EDGE,"E32.1.5")])]});var subQ11=sQuery(id+"F0.wireOp",EDGE,"E0");Q1=makeQuery(id+"F13.boolean.opBoolean","SPLIT",FACE,{"disambiguationData":[TD([makeQuery(id+"F10.boolean.opBoolean","COPY",FACE,{"derivedFrom":subQ0})])],"derivedFrom":makeQuery(id+"F10.boolean.opBoolean","SPLIT",FACE,{"disambiguationData":[TD([subQ0])],"derivedFrom":makeQuery(id+"F9.opExtrude","SWEPT_FACE",FACE,{"disambiguationData":[OSD([subQ11])]})})});}
            var Q2;
            {var subQ0=makeQuery(id+"F10.opExtrude","SWEPT_FACE",FACE,{"disambiguationData":[OSD([sQuery(id+"F3.wireOp",EDGE,"E32.2.7")])]});var subQ11=sQuery(id+"F0.wireOp",EDGE,"E0");Q2=makeQuery(id+"F13.boolean.opBoolean","SPLIT",FACE,{"disambiguationData":[TD([makeQuery(id+"F10.boolean.opBoolean","COPY",FACE,{"derivedFrom":subQ0})])],"derivedFrom":makeQuery(id+"F10.boolean.opBoolean","SPLIT",FACE,{"disambiguationData":[TD([makeQuery(id+"F10.opExtrude","SWEPT_FACE",FACE,{"disambiguationData":[OSD([sQuery(id+"F3.wireOp",EDGE,"E32.1.5")])]})])],"derivedFrom":makeQuery(id+"F9.opExtrude","SWEPT_FACE",FACE,{"disambiguationData":[OSD([subQ11])]})})});}
            var Q3;
            {var subQ10=makeQuery(id+"F10.opExtrude","SWEPT_FACE",FACE,{"disambiguationData":[OSD([sQuery(id+"F3.wireOp",EDGE,"E32.2.5")])]});var subQ11=sQuery(id+"F0.wireOp",EDGE,"E0");Q3=makeQuery(id+"F13.boolean.opBoolean","SPLIT",FACE,{"disambiguationData":[TD([makeQuery(id+"F10.boolean.opBoolean","COPY",FACE,{"derivedFrom":subQ10})])],"derivedFrom":makeQuery(id+"F10.boolean.opBoolean","SPLIT",FACE,{"disambiguationData":[TD([subQ10])],"derivedFrom":makeQuery(id+"F9.opExtrude","SWEPT_FACE",FACE,{"disambiguationData":[OSD([subQ11])]})})});}
            var Q4;
            {var subQ10=makeQuery(id+"F10.opExtrude","SWEPT_FACE",FACE,{"disambiguationData":[OSD([sQuery(id+"F3.wireOp",EDGE,"E32.3.7")])]});var subQ11=sQuery(id+"F0.wireOp",EDGE,"E0");Q4=makeQuery(id+"F13.boolean.opBoolean","SPLIT",FACE,{"disambiguationData":[TD([makeQuery(id+"F10.boolean.opBoolean","COPY",FACE,{"derivedFrom":subQ10})])],"derivedFrom":makeQuery(id+"F10.boolean.opBoolean","SPLIT",FACE,{"disambiguationData":[TD([makeQuery(id+"F10.opExtrude","SWEPT_FACE",FACE,{"disambiguationData":[OSD([sQuery(id+"F3.wireOp",EDGE,"E32.2.5")])]})])],"derivedFrom":makeQuery(id+"F9.opExtrude","SWEPT_FACE",FACE,{"disambiguationData":[OSD([subQ11])]})})});}
            var Q5;
            {var subQ10=makeQuery(id+"F10.opExtrude","SWEPT_FACE",FACE,{"disambiguationData":[OSD([sQuery(id+"F3.wireOp",EDGE,"E32.3.5")])]});var subQ11=sQuery(id+"F0.wireOp",EDGE,"E0");Q5=makeQuery(id+"F13.boolean.opBoolean","SPLIT",FACE,{"disambiguationData":[TD([makeQuery(id+"F10.boolean.opBoolean","COPY",FACE,{"derivedFrom":subQ10})])],"derivedFrom":makeQuery(id+"F10.boolean.opBoolean","SPLIT",FACE,{"disambiguationData":[TD([makeQuery(id+"F10.opExtrude","SWEPT_FACE",FACE,{"disambiguationData":[OSD([sQuery(id+"F3.wireOp",EDGE,"E31")])]})])],"derivedFrom":makeQuery(id+"F9.opExtrude","SWEPT_FACE",FACE,{"disambiguationData":[OSD([subQ11])]})})});}
            var Q6;
            {var subQ10=sQuery(id+"F0.wireOp",EDGE,"E0");var subQ12=makeQuery(id+"F10.opExtrude","SWEPT_FACE",FACE,{"disambiguationData":[OSD([sQuery(id+"F3.wireOp",EDGE,"E31")])]});Q6=makeQuery(id+"F13.boolean.opBoolean","SPLIT",FACE,{"disambiguationData":[TD([makeQuery(id+"F10.boolean.opBoolean","COPY",FACE,{"derivedFrom":subQ12})])],"derivedFrom":makeQuery(id+"F10.boolean.opBoolean","SPLIT",FACE,{"disambiguationData":[TD([subQ12])],"derivedFrom":makeQuery(id+"F9.opExtrude","SWEPT_FACE",FACE,{"disambiguationData":[OSD([subQ10])]})})});}
            var Q7;
            {var subQ10=makeQuery(id+"F10.opExtrude","SWEPT_FACE",FACE,{"disambiguationData":[OSD([sQuery(id+"F3.wireOp",EDGE,"E30")])]});var subQ11=sQuery(id+"F0.wireOp",EDGE,"E0");Q7=makeQuery(id+"F13.boolean.opBoolean","SPLIT",FACE,{"disambiguationData":[TD([makeQuery(id+"F10.boolean.opBoolean","COPY",FACE,{"derivedFrom":subQ10})])],"derivedFrom":makeQuery(id+"F10.boolean.opBoolean","SPLIT",FACE,{"disambiguationData":[TD([subQ10])],"derivedFrom":makeQuery(id+"F9.opExtrude","SWEPT_FACE",FACE,{"disambiguationData":[OSD([subQ11])]})})});}
            var Q8;
            {var subQ1=makeQuery(id+"F10.opExtrude","SWEPT_FACE",FACE,{"disambiguationData":[OSD([sQuery(id+"F3.wireOp",EDGE,"E32.1.7")])]});var subQ2=sQuery(id+"F0.wireOp",EDGE,"E0");Q8=makeQuery(id+"F13.boolean.opBoolean","SPLIT",FACE,{"disambiguationData":[TD([makeQuery(id+"F10.boolean.opBoolean","COPY",FACE,{"derivedFrom":subQ1})])],"derivedFrom":makeQuery(id+"F10.boolean.opBoolean","SPLIT",FACE,{"disambiguationData":[TD([makeQuery(id+"F10.opExtrude","SWEPT_FACE",FACE,{"disambiguationData":[OSD([sQuery(id+"F3.wireOp",EDGE,"E30")])]})])],"derivedFrom":makeQuery(id+"F9.opExtrude","SWEPT_FACE",FACE,{"disambiguationData":[OSD([subQ2])]})})});}
            var Q9;
            Q9=makeQuery(id+"F9.opExtrude","CAP_FACE",FACE,{"disambiguationData":[OSD([sQuery(id+"F0.wireOp",EDGE,"E0")])],"isStart":true});
            var Q10;
            {var subQ0=sQuery(id+"F4.wireOp",EDGE,"E45.3.3");var subQ1=sQuery(id+"F4.wireOp",EDGE,"E45.3.1");var subQ2=sQuery(id+"F4.wireOp",EDGE,"E45.3.4");Q10=makeQuery(id+"F13.boolean.opBoolean","SPLIT",FACE,{"disambiguationData":[TD([makeQuery(id+"F11.boolean.opBoolean","COPY",FACE,{"derivedFrom":makeQuery(id+"F11.opExtrude","SWEPT_FACE",FACE,{"disambiguationData":[OSD([subQ1])]})})])],"derivedFrom":makeQuery(id+"F12.boolean.opBoolean","COPY",FACE,{"derivedFrom":makeQuery(id+"F12.opExtrude","CAP_FACE",FACE,{"disambiguationData":[OSD([sQuery(id+"F4.wireOp",EDGE,"E45.3.0"),subQ1,sQuery(id+"F4.wireOp",EDGE,"E45.3.2"),subQ0,subQ2,sQuery(id+"F4.wireOp",EDGE,"E45.3.5"),sQuery(id+"F4.wireOp",EDGE,"E45.3.8"),sQuery(id+"F4.wireOp",EDGE,"E45.3.9"),sQuery(id+"F4.wireOp",EDGE,"E45.3.10"),sQuery(id+"F4.wireOp",EDGE,"E45.3.11")])],"isStart":true})})});}
            var Q11;
            {var subQ0=sQuery(id+"F4.wireOp",EDGE,"E45.3.9");var subQ1=sQuery(id+"F4.wireOp",EDGE,"E45.3.5");var subQ2=sQuery(id+"F4.wireOp",EDGE,"E45.3.10");Q11=makeQuery(id+"F13.boolean.opBoolean","SPLIT",FACE,{"disambiguationData":[TD([makeQuery(id+"F11.boolean.opBoolean","COPY",FACE,{"derivedFrom":makeQuery(id+"F11.opExtrude","SWEPT_FACE",FACE,{"disambiguationData":[OSD([subQ2])]})})])],"derivedFrom":makeQuery(id+"F12.boolean.opBoolean","COPY",FACE,{"derivedFrom":makeQuery(id+"F12.opExtrude","CAP_FACE",FACE,{"disambiguationData":[OSD([sQuery(id+"F4.wireOp",EDGE,"E45.3.0"),sQuery(id+"F4.wireOp",EDGE,"E45.3.1"),sQuery(id+"F4.wireOp",EDGE,"E45.3.2"),sQuery(id+"F4.wireOp",EDGE,"E45.3.3"),sQuery(id+"F4.wireOp",EDGE,"E45.3.4"),subQ1,sQuery(id+"F4.wireOp",EDGE,"E45.3.8"),subQ0,subQ2,sQuery(id+"F4.wireOp",EDGE,"E45.3.11")])],"isStart":true})})});}
            var Q12;
            {var subQ0=sQuery(id+"F4.wireOp",EDGE,"E45.2.3");var subQ1=sQuery(id+"F4.wireOp",EDGE,"E45.2.1");var subQ2=sQuery(id+"F4.wireOp",EDGE,"E45.2.4");Q12=makeQuery(id+"F13.boolean.opBoolean","SPLIT",FACE,{"disambiguationData":[TD([makeQuery(id+"F11.boolean.opBoolean","COPY",FACE,{"derivedFrom":makeQuery(id+"F11.opExtrude","SWEPT_FACE",FACE,{"disambiguationData":[OSD([subQ1])]})})])],"derivedFrom":makeQuery(id+"F12.boolean.opBoolean","COPY",FACE,{"derivedFrom":makeQuery(id+"F12.opExtrude","CAP_FACE",FACE,{"disambiguationData":[OSD([sQuery(id+"F4.wireOp",EDGE,"E45.2.0"),subQ1,sQuery(id+"F4.wireOp",EDGE,"E45.2.2"),subQ0,subQ2,sQuery(id+"F4.wireOp",EDGE,"E45.2.5"),sQuery(id+"F4.wireOp",EDGE,"E45.2.8"),sQuery(id+"F4.wireOp",EDGE,"E45.2.9"),sQuery(id+"F4.wireOp",EDGE,"E45.2.10"),sQuery(id+"F4.wireOp",EDGE,"E45.2.11")])],"isStart":true})})});}
            var Q13;
            {var subQ0=sQuery(id+"F4.wireOp",EDGE,"E45.2.9");var subQ1=sQuery(id+"F4.wireOp",EDGE,"E45.2.5");var subQ2=sQuery(id+"F4.wireOp",EDGE,"E45.2.10");Q13=makeQuery(id+"F13.boolean.opBoolean","SPLIT",FACE,{"disambiguationData":[TD([makeQuery(id+"F11.boolean.opBoolean","COPY",FACE,{"derivedFrom":makeQuery(id+"F11.opExtrude","SWEPT_FACE",FACE,{"disambiguationData":[OSD([subQ2])]})})])],"derivedFrom":makeQuery(id+"F12.boolean.opBoolean","COPY",FACE,{"derivedFrom":makeQuery(id+"F12.opExtrude","CAP_FACE",FACE,{"disambiguationData":[OSD([sQuery(id+"F4.wireOp",EDGE,"E45.2.0"),sQuery(id+"F4.wireOp",EDGE,"E45.2.1"),sQuery(id+"F4.wireOp",EDGE,"E45.2.2"),sQuery(id+"F4.wireOp",EDGE,"E45.2.3"),sQuery(id+"F4.wireOp",EDGE,"E45.2.4"),subQ1,sQuery(id+"F4.wireOp",EDGE,"E45.2.8"),subQ0,subQ2,sQuery(id+"F4.wireOp",EDGE,"E45.2.11")])],"isStart":true})})});}
            var Q14;
            {var subQ0=sQuery(id+"F4.wireOp",EDGE,"E45.1.3");var subQ1=sQuery(id+"F4.wireOp",EDGE,"E45.1.1");var subQ2=sQuery(id+"F4.wireOp",EDGE,"E45.1.4");Q14=makeQuery(id+"F13.boolean.opBoolean","SPLIT",FACE,{"disambiguationData":[TD([makeQuery(id+"F11.boolean.opBoolean","COPY",FACE,{"derivedFrom":makeQuery(id+"F11.opExtrude","SWEPT_FACE",FACE,{"disambiguationData":[OSD([subQ1])]})})])],"derivedFrom":makeQuery(id+"F12.boolean.opBoolean","COPY",FACE,{"derivedFrom":makeQuery(id+"F12.opExtrude","CAP_FACE",FACE,{"disambiguationData":[OSD([sQuery(id+"F4.wireOp",EDGE,"E45.1.0"),subQ1,sQuery(id+"F4.wireOp",EDGE,"E45.1.2"),subQ0,subQ2,sQuery(id+"F4.wireOp",EDGE,"E45.1.5"),sQuery(id+"F4.wireOp",EDGE,"E45.1.8"),sQuery(id+"F4.wireOp",EDGE,"E45.1.9"),sQuery(id+"F4.wireOp",EDGE,"E45.1.10"),sQuery(id+"F4.wireOp",EDGE,"E45.1.11")])],"isStart":true})})});}
            var Q15;
            {var subQ0=sQuery(id+"F4.wireOp",EDGE,"E45.1.5");var subQ1=sQuery(id+"F4.wireOp",EDGE,"E45.1.10");var subQ2=sQuery(id+"F4.wireOp",EDGE,"E45.1.9");Q15=makeQuery(id+"F13.boolean.opBoolean","SPLIT",FACE,{"disambiguationData":[TD([makeQuery(id+"F11.boolean.opBoolean","COPY",FACE,{"derivedFrom":makeQuery(id+"F11.opExtrude","SWEPT_FACE",FACE,{"disambiguationData":[OSD([subQ1])]})})])],"derivedFrom":makeQuery(id+"F12.boolean.opBoolean","COPY",FACE,{"derivedFrom":makeQuery(id+"F12.opExtrude","CAP_FACE",FACE,{"disambiguationData":[OSD([sQuery(id+"F4.wireOp",EDGE,"E45.1.0"),sQuery(id+"F4.wireOp",EDGE,"E45.1.1"),sQuery(id+"F4.wireOp",EDGE,"E45.1.2"),sQuery(id+"F4.wireOp",EDGE,"E45.1.3"),sQuery(id+"F4.wireOp",EDGE,"E45.1.4"),subQ0,sQuery(id+"F4.wireOp",EDGE,"E45.1.8"),subQ2,subQ1,sQuery(id+"F4.wireOp",EDGE,"E45.1.11")])],"isStart":true})})});}
            var Q16;
            {var subQ0=sQuery(id+"F4.wireOp",EDGE,"E34.0");var subQ1=sQuery(id+"F4.wireOp",EDGE,"E38.0");var subQ2=sQuery(id+"F4.wireOp",EDGE,"E44.trimOffspring");Q16=makeQuery(id+"F13.boolean.opBoolean","SPLIT",FACE,{"disambiguationData":[TD([makeQuery(id+"F11.boolean.opBoolean","COPY",FACE,{"derivedFrom":makeQuery(id+"F11.opExtrude","SWEPT_FACE",FACE,{"disambiguationData":[OSD([subQ0])]})})])],"derivedFrom":makeQuery(id+"F12.boolean.opBoolean","COPY",FACE,{"derivedFrom":makeQuery(id+"F12.opExtrude","CAP_FACE",FACE,{"disambiguationData":[OSD([subQ0,sQuery(id+"F4.wireOp",EDGE,"E35.0"),sQuery(id+"F4.wireOp",EDGE,"E37.0"),subQ1,sQuery(id+"F4.wireOp",EDGE,"E39.trimOffspring"),sQuery(id+"F4.wireOp",EDGE,"E40.0"),sQuery(id+"F4.wireOp",EDGE,"E41.0"),sQuery(id+"F4.wireOp",EDGE,"E42"),sQuery(id+"F4.wireOp",EDGE,"E43"),subQ2])],"isStart":true})})});}
            var Q17;
            {var subQ0=sQuery(id+"F4.wireOp",EDGE,"E35.0");var subQ1=sQuery(id+"F4.wireOp",EDGE,"E39.trimOffspring");var subQ2=sQuery(id+"F4.wireOp",EDGE,"E41.0");Q17=makeQuery(id+"F13.boolean.opBoolean","SPLIT",FACE,{"disambiguationData":[TD([makeQuery(id+"F11.boolean.opBoolean","COPY",FACE,{"derivedFrom":makeQuery(id+"F11.opExtrude","SWEPT_FACE",FACE,{"disambiguationData":[OSD([subQ0])]})})])],"derivedFrom":makeQuery(id+"F12.boolean.opBoolean","COPY",FACE,{"derivedFrom":makeQuery(id+"F12.opExtrude","CAP_FACE",FACE,{"disambiguationData":[OSD([sQuery(id+"F4.wireOp",EDGE,"E34.0"),subQ0,sQuery(id+"F4.wireOp",EDGE,"E37.0"),sQuery(id+"F4.wireOp",EDGE,"E38.0"),subQ1,sQuery(id+"F4.wireOp",EDGE,"E40.0"),subQ2,sQuery(id+"F4.wireOp",EDGE,"E42"),sQuery(id+"F4.wireOp",EDGE,"E43"),sQuery(id+"F4.wireOp",EDGE,"E44.trimOffspring")])],"isStart":true})})});}
            shell(context, id + "F20", {"entities" : qUnion([Q0, Q1, Q2, Q3, Q4, Q5, Q6, Q7, Q8, Q9, Q10, Q11, Q12, Q13, Q14, Q15, Q16, Q17]), "thickness" : 1 * mm});
        }
        {
            var Q0;
            Q0 = qSketchRegion(id + "F15", true);
            extrude(context, id + "F21", {"entities" : qUnion([Q0]), "operationType" : NewBodyOperationType.ADD, "depth" : 46 * mm});
        }
        {
            var Q0;
            Q0 = qSketchRegion(id + "F5", true);
            extrude(context, id + "F22", {"entities" : qUnion([Q0]), "operationType" : NewBodyOperationType.REMOVE, "endBound" : BoundingType.THROUGH_ALL, "depth" : 29.85 * mm, "hasSecondDirection" : true, "secondDirectionOppositeDirection" : true, "secondDirectionDepth" : 9 * mm});
        }
        {
            var Q0;
            Q0=qCreatedBy(id+"F17.planeOp",FACE);
            var sketch = newSketch(context, id + "F23", { "sketchPlane" : qUnion([Q0])});
            skCircle(sketch, "E99.0", {"center": v(0, 0) * mm, "radius": 27.6 * mm});
            skCircle(sketch, "E100", {"center": v(0, 0) * mm, "radius": 7 * mm});
            skCircle(sketch, "E101", {"center": v(13.15, 13.15) * mm, "radius": 7 * mm});
            skCircle(sketch, "E102.1.0", {"center": v(-13.15, 13.15) * mm, "radius": 7 * mm});
            skCircle(sketch, "E102.2.0", {"center": v(-13.15, -13.15) * mm, "radius": 7 * mm});
            skCircle(sketch, "E102.3.0", {"center": v(13.15, -13.15) * mm, "radius": 7 * mm});
            skSolve(sketch);
        }
        {
            var Q0;
            Q0=qCreatedBy(id+"F17.planeOp",FACE);
            var sketch = newSketch(context, id + "F24", { "sketchPlane" : qUnion([Q0])});
            skArc(sketch, "E103.0", {"start": v(-9.18, 3.98) * mm, "mid": v(-10, 0) * mm, "end": v(-9.18, -3.98) * mm});
            skArc(sketch, "E104.0", {"start": v(11.29, 22.98) * mm, "mid": v(4.32, 17.83) * mm, "end": v(3.98, 9.18) * mm});
            skArc(sketch, "E105.0", {"start": v(22.98, -11.29) * mm, "mid": v(17.83, -4.32) * mm, "end": v(9.18, -3.98) * mm});
            skArc(sketch, "E106.0", {"start": v(-11.29, -22.98) * mm, "mid": v(-4.32, -17.83) * mm, "end": v(-3.98, -9.18) * mm});
            skArc(sketch, "E107.0", {"start": v(-22.98, 11.29) * mm, "mid": v(-17.83, 4.32) * mm, "end": v(-9.18, 3.98) * mm});
            skArc(sketch, "E108.0", {"start": v(-22.98, 11.29) * mm, "mid": v(-25.6, 0) * mm, "end": v(-22.98, -11.29) * mm});
            skCircle(sketch, "E109", {"center": v(-13.15, -13.15) * mm, "radius": 7 * mm});
            skCircle(sketch, "E110", {"center": v(-13.15, 13.15) * mm, "radius": 7 * mm});
            skCircle(sketch, "E111", {"center": v(13.15, 13.15) * mm, "radius": 7 * mm});
            skCircle(sketch, "E112", {"center": v(0, 0) * mm, "radius": 7 * mm});
            skCircle(sketch, "E113", {"center": v(0, 0) * mm, "radius": 27.6 * mm});
            skCircle(sketch, "E114", {"center": v(13.15, -13.15) * mm, "radius": 7 * mm});
            skArc(sketch, "E115.trimOffspring", {"start": v(-3.98, 9.18) * mm, "mid": v(-4.32, 17.83) * mm, "end": v(-11.29, 22.98) * mm});
            skArc(sketch, "E116.trimOffspring", {"start": v(11.29, 22.98) * mm, "mid": v(0, 25.6) * mm, "end": v(-11.29, 22.98) * mm});
            skArc(sketch, "E117.trimOffspring", {"start": v(3.98, 9.18) * mm, "mid": v(0, 10) * mm, "end": v(-3.98, 9.18) * mm});
            skArc(sketch, "E118.trimOffspring", {"start": v(9.18, 3.98) * mm, "mid": v(17.83, 4.32) * mm, "end": v(22.98, 11.29) * mm});
            skArc(sketch, "E119.trimOffspring", {"start": v(9.18, -3.98) * mm, "mid": v(10, 0) * mm, "end": v(9.18, 3.98) * mm});
            skArc(sketch, "E120.trimOffspring", {"start": v(3.98, -9.18) * mm, "mid": v(4.32, -17.83) * mm, "end": v(11.29, -22.98) * mm});
            skArc(sketch, "E121.trimOffspring", {"start": v(22.98, -11.29) * mm, "mid": v(25.6, 0) * mm, "end": v(22.98, 11.29) * mm});
            skArc(sketch, "E122.trimOffspring", {"start": v(-9.18, -3.98) * mm, "mid": v(-17.83, -4.32) * mm, "end": v(-22.98, -11.29) * mm});
            skArc(sketch, "E123.trimOffspring", {"start": v(-3.98, -9.18) * mm, "mid": v(0, -10) * mm, "end": v(3.98, -9.18) * mm});
            skArc(sketch, "E124.trimOffspring", {"start": v(-11.29, -22.98) * mm, "mid": v(0, -25.6) * mm, "end": v(11.29, -22.98) * mm});
            skSolve(sketch);
        }
        {
            var Q0;
            Q0 = qSketchRegion(id + "F24", true);
            extrude(context, id + "F25", {"entities" : qUnion([Q0]), "operationType" : NewBodyOperationType.ADD, "depth" : 2 * mm});
        }
    });
